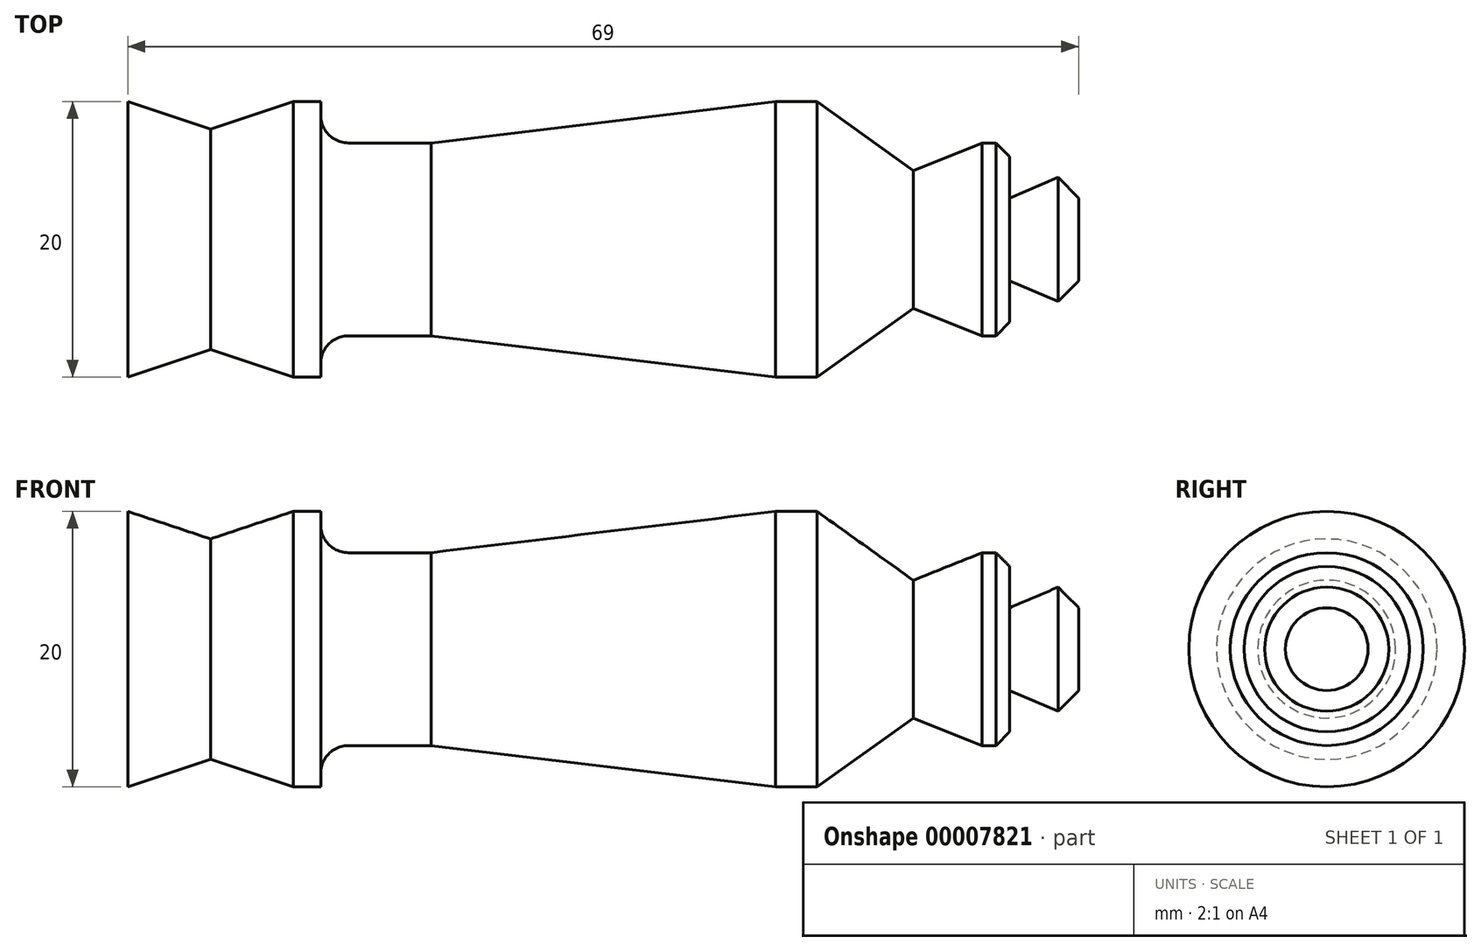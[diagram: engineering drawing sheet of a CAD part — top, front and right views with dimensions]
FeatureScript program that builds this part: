
annotation { "Feature Type Name" : "Feature", "Feature Type Description" : "" }
export const myFeature = defineFeature(function(context is Context, id is Id, definition is map)
    precondition{}
    {
        {
            var Q0;
            Q0=qCreatedBy(makeId("Front.planeOp"),FACE);
            var sketch = newSketch(context, id + "F0", { "sketchPlane" : qUnion([Q0])});
            skLineSegment(sketch, "E0", {"start": v(-46.1, 0) * mm, "end": v(43.9, 0) * mm});
            skLineSegment(sketch, "E1", {"start": v(40.9, 0) * mm, "end": v(40.9, -4.5) * mm});
            skLineSegment(sketch, "E2", {"start": v(40.9, -4.5) * mm, "end": v(39.4, -4.5) * mm});
            skLineSegment(sketch, "E3", {"start": v(39.4, -4.5) * mm, "end": v(35.9, -3) * mm});
            skLineSegment(sketch, "E4", {"start": v(35.9, -3) * mm, "end": v(35.9, -7) * mm});
            skLineSegment(sketch, "E5", {"start": v(35.9, -7) * mm, "end": v(33.9, -7) * mm});
            skLineSegment(sketch, "E6", {"start": v(33.9, -7) * mm, "end": v(28.9, -5) * mm});
            skLineSegment(sketch, "E7", {"start": v(28.9, -5) * mm, "end": v(21.9, -10) * mm});
            skLineSegment(sketch, "E8", {"start": v(21.9, -10) * mm, "end": v(18.9, -10) * mm});
            skLineSegment(sketch, "E9", {"start": v(18.9, -10) * mm, "end": v(-6.1, -7) * mm});
            skLineSegment(sketch, "E10", {"start": v(-6.1, -7) * mm, "end": v(-14.1, -7) * mm});
            skLineSegment(sketch, "E11", {"start": v(-14.1, -7) * mm, "end": v(-14.1, -10) * mm});
            skLineSegment(sketch, "E12", {"start": v(-14.1, -10) * mm, "end": v(-16.1, -10) * mm});
            skLineSegment(sketch, "E13", {"start": v(-16.1, -10) * mm, "end": v(-22.1, -8) * mm});
            skLineSegment(sketch, "E14", {"start": v(-22.1, -8) * mm, "end": v(-28.1, -10) * mm});
            skLineSegment(sketch, "E15", {"start": v(-28.1, -10) * mm, "end": v(-28.1, 0) * mm});
            skSolve(sketch);
        }
        {
            var Q0;
            {var subQ1=sQuery(id+"F0.wireOp",EDGE,"E1");Q0=makeQuery(id+"F0.imprint","IMPRINT",FACE,{"disambiguationData":[TD([[makeQuery(id+"F0.imprint","IMPRINT",EDGE,{"derivedFrom":subQ1}),-1.0]])]});}
            var Q1;
            Q1=sQuery(id+"F0.wireOp",EDGE,"E0");
            revolve(context, id + "F1", {"entities" : qUnion([Q0]), "axis" : qUnion([Q1]), "revolveType" : RevolveType.FULL});
        }
        {
            var Q0;
            Q0=makeQuery(id+"F1.opRevolve","SWEPT_EDGE",EDGE,{"disambiguationData":[OSD([sQuery(id+"F0.wireOp",EDGE,"E1"),sQuery(id+"F0.wireOp",EDGE,"E2")])]});
            chamfer(context, id + "F2", {"entities" : qUnion([Q0]), "width" : 1.5 * mm});
        }
        {
            var Q0;
            Q0=makeQuery(id+"F1.opRevolve","SWEPT_EDGE",EDGE,{"disambiguationData":[OSD([sQuery(id+"F0.wireOp",EDGE,"E4"),sQuery(id+"F0.wireOp",EDGE,"E5")])]});
            chamfer(context, id + "F3", {"entities" : qUnion([Q0]), "width" : 1 * mm});
        }
        {
            var Q0;
            Q0=makeQuery(id+"F1.opRevolve","SWEPT_EDGE",EDGE,{"disambiguationData":[OSD([sQuery(id+"F0.wireOp",EDGE,"E10"),sQuery(id+"F0.wireOp",EDGE,"E11")])]});
            fillet(context, id + "F4", {"entities" : qUnion([Q0]), "radius" : 2 * mm, "allowEdgeOverflow" : false});
        }
    });
